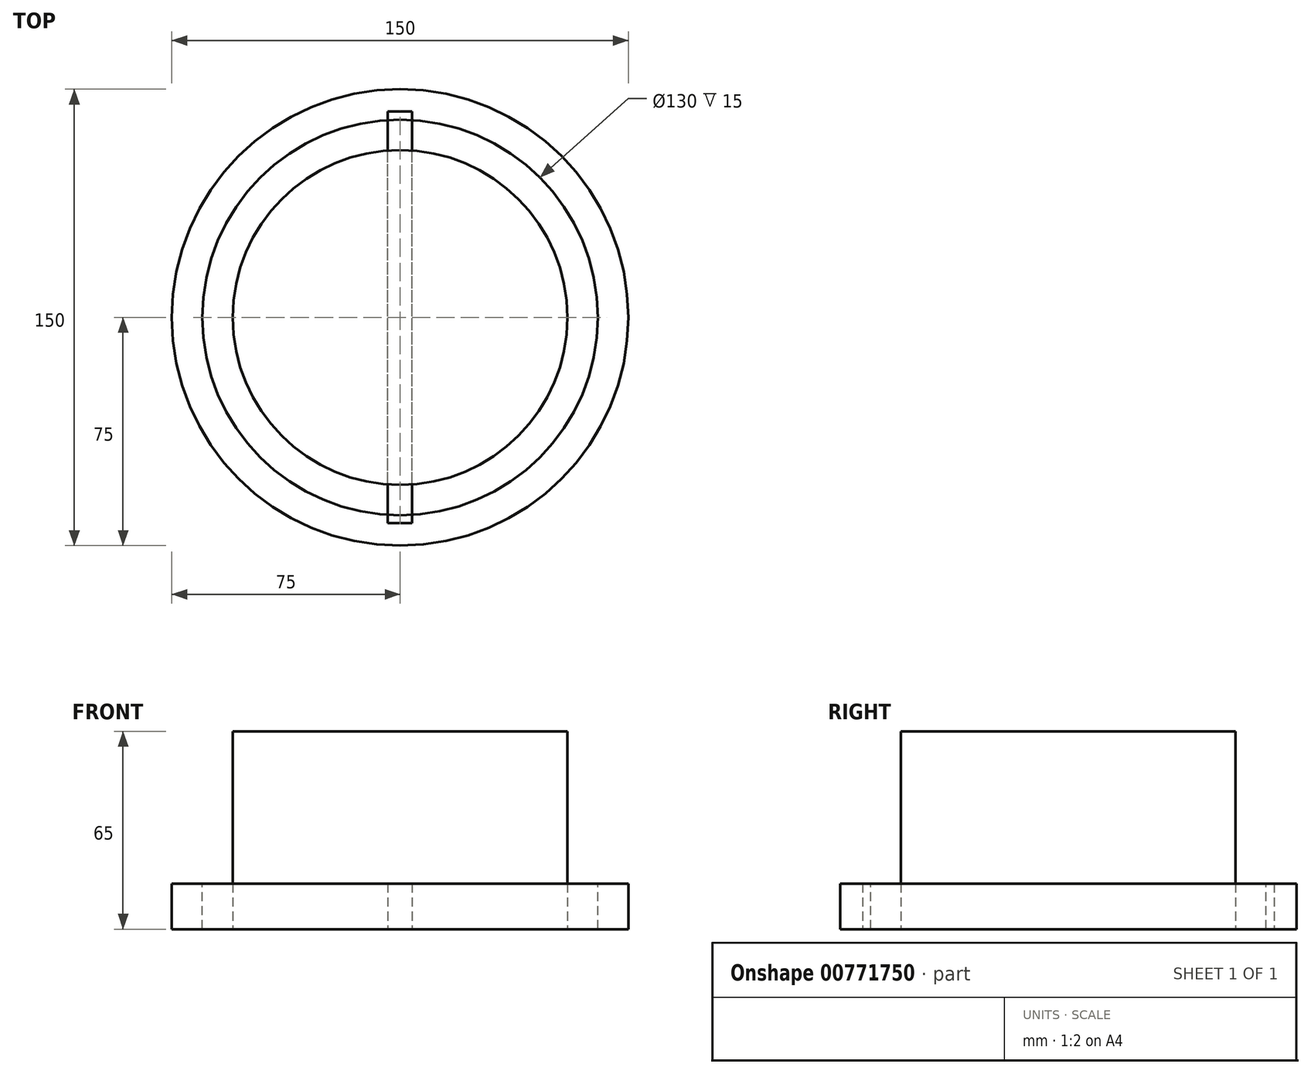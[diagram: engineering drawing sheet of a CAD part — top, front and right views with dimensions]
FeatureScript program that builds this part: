
annotation { "Feature Type Name" : "Feature", "Feature Type Description" : "" }
export const myFeature = defineFeature(function(context is Context, id is Id, definition is map)
    precondition{}
    {
        {
            var Q0;
            Q0=qCreatedBy(makeId("Top.planeOp"),FACE);
            var sketch = newSketch(context, id + "F0", { "sketchPlane" : qUnion([Q0])});
            skCircle(sketch, "E0", {"center": v(0, 0) * mm, "radius": 75 * mm});
            skSolve(sketch);
        }
        {
            var Q0;
            Q0=makeQuery(id+"F0.imprint","IMPRINT",FACE,{"disambiguationData":[TD([[makeQuery(id+"F0.imprint","IMPRINT",EDGE,{"derivedFrom":sQuery(id+"F0.wireOp",EDGE,"E0")}),1.0]])]});
            extrude(context, id + "F1", {"entities" : qUnion([Q0]), "depth" : 15 * mm, "offsetDistance" : 25 * mm});
        }
        {
            var Q0;
            Q0=makeQuery(id+"F1.opExtrude","CAP_FACE",FACE,{"disambiguationData":[OSD([sQuery(id+"F0.wireOp",EDGE,"E0")])],"isStart":false});
            var sketch = newSketch(context, id + "F2", { "sketchPlane" : qUnion([Q0])});
            skCircle(sketch, "E1", {"center": v(0, 0) * mm, "radius": 65 * mm});
            skSolve(sketch);
        }
        {
            var Q0;
            Q0=makeQuery(id+"F2.imprint","IMPRINT",FACE,{"disambiguationData":[TD([[makeQuery(id+"F2.imprint","IMPRINT",EDGE,{"derivedFrom":sQuery(id+"F2.wireOp",EDGE,"E1")}),1.0]])]});
            extrude(context, id + "F3", {"entities" : qUnion([Q0]), "operationType" : NewBodyOperationType.REMOVE, "oppositeDirection" : true, "depth" : 21.3 * mm, "offsetDistance" : 25 * mm});
        }
        {
            var Q0;
            Q0=qCreatedBy(makeId("Top.planeOp"),FACE);
            var sketch = newSketch(context, id + "F4", { "sketchPlane" : qUnion([Q0])});
            skCircle(sketch, "E2", {"center": v(0, 0) * mm, "radius": 55 * mm});
            skSolve(sketch);
        }
        {
            var Q0;
            Q0=makeQuery(id+"F4.imprint","IMPRINT",FACE,{"disambiguationData":[TD([[makeQuery(id+"F4.imprint","IMPRINT",EDGE,{"derivedFrom":sQuery(id+"F4.wireOp",EDGE,"E2")}),1.0]])]});
            extrude(context, id + "F5", {"entities" : qUnion([Q0]), "depth" : 15 * mm, "offsetDistance" : 25 * mm});
        }
        {
            var Q0;
            Q0=qCreatedBy(makeId("Top.planeOp"),FACE);
            var sketch = newSketch(context, id + "F6", { "sketchPlane" : qUnion([Q0])});
            skLineSegment(sketch, "E3.bottom", {"start": v(4, -67.63) * mm, "end": v(-4, -67.63) * mm});
            skLineSegment(sketch, "E3.top", {"start": v(4, 67.63) * mm, "end": v(-4, 67.63) * mm});
            skLineSegment(sketch, "E3.left", {"start": v(4, -67.63) * mm, "end": v(4, 67.63) * mm});
            skLineSegment(sketch, "E3.right", {"start": v(-4, -67.63) * mm, "end": v(-4, 67.63) * mm});
            skPoint(sketch, "E3.middle", {"position": v(0, 0) * mm});
            skSolve(sketch);
        }
        {
            var Q0;
            Q0=makeQuery(id+"F6.imprint","IMPRINT",FACE,{"disambiguationData":[TD([[makeQuery(id+"F6.imprint","IMPRINT",EDGE,{"derivedFrom":sQuery(id+"F6.wireOp",EDGE,"E3.bottom")}),-1.0]])]});
            extrude(context, id + "F7", {"entities" : qUnion([Q0]), "depth" : 15 * mm, "offsetDistance" : 25 * mm});
        }
        {
            var Q0;
            Q0=makeQuery(id+"F5.opExtrude","CAP_FACE",FACE,{"disambiguationData":[OSD([sQuery(id+"F4.wireOp",EDGE,"E2")])],"isStart":false});
            extrude(context, id + "F8", {"entities" : qUnion([Q0]), "depth" : 50 * mm, "offsetDistance" : 25 * mm});
        }
    });
